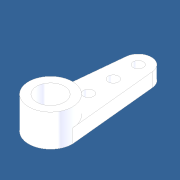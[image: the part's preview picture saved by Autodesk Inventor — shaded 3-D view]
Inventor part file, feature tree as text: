
AUTODESK INVENTOR PART (.ipt)
format: ipt  version: unknown  size: 201,216 bytes
history: native  units: mm
features: extrude x3, sketch x3, pattern_linear x1
ambient origin geometry x8: Origin, YZ Plane, XZ Plane, XY Plane, X Axis, Y Axis, Z Axis, Center Point
bodies: Solid1 (feature_tree)
feature tree (7):
  extrude  "Extrusion1"  Depth=6.0mm
  extrude  "Extrusion3"  Depth=12.0mm
  extrude  "Extrusion4"  Depth=2.5mm TaperAngle=0.0deg
  pattern_linear  "Rectangular Pattern2"  Spacing1=12.0mm  [1 undecoded]
  sketch  "Sketch1"  dims[d0=3.8mm d1=6.0mm]
  sketch  "Sketch3"  dims[d2=3.6mm d3=12.0mm]
  sketch  "Sketch4"  dims[d4=1.9mm d5=0.0mm d12=2.5mm d13=0.0mm d14=12.0mm d15=1.4mm d16=10.0mm d17=0.0mm d18=30.0mm d20=3.4mm]
note: 1 required parameter value undecoded (feature->parameter linkage not recoverable at this tier; creation-order binding heuristic only, values carry confidence <= 0.55)
